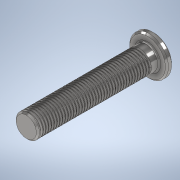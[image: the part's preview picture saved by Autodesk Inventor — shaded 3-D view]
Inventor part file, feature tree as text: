
AUTODESK INVENTOR PART (.ipt)
format: ipt  version: 2021 (Build 250183000, 183)  size: 1,093,632 bytes
history: native  units: in
note: dims shown in document units (in); Inventor stores cm internally (conversion verified against a paired STEP export)
features: sketch x5, extrude x4, chamfer x3, fillet x2, helix x1, projected_geometry x1
ambient origin geometry x8: Origin, YZ Plane, XZ Plane, XY Plane, X Axis, Y Axis, Z Axis, Center Point
bodies: Solid2 (feature_tree)
feature tree (16):
  extrude  "Extrusion3"  Depth=0.3085in TaperAngle=0.0deg
  chamfer  "Chamfer1"  Distance=0.0039in Angle=45.0deg
  extrude  "Extrusion4"  Depth=0.0157in TaperAngle=0.0deg
  fillet  "Fillet1"  Radius=0.0039in
  chamfer  "Chamfer2"  Distance=0.0039in Angle=45.0deg
  chamfer  "Chamfer3"  Distance=0.0039in Angle=45.0deg
  extrude  "Extrusion5"  Depth=0.0118in
  helix  "Coil1"  [1 undecoded]
  fillet  "Fillet3"  Radius=0.0591in
  extrude  "Extrusion6"  TaperAngle=60.0deg  [1 undecoded]
  sketch  "Sketch3"  dims[d6=0.0591in d7=0.3085in d8=0.0in d9=0.0039in d10=0.0787in d11=45.0deg]
  sketch  "Sketch4"  dims[d12=0.0984in d13=0.0157in d14=0.0in d15=0.0039in d17=0.0039in d18=0.0787in d19=45.0deg d20=0.0039in d21=0.0787in d22=45.0deg]
  sketch  "Sketch5"  dims[d23=0.0079in d24=0.0in d25=0.0118in d26=0.0118in d27=0.0591in]
  sketch  "Sketch6"  dims[d32=0.0197in d33=60.0deg]
  sketch  "Sketch7"  dims[d35=0.0039in d36=0.002in d37=0.0071in d38=0.3937in d39=15.5512in d40=0.0in d41=90.0deg d42=90.0deg d43=0.0in d44=0.0in d45=0.0039in d46=0.0236in d47=0.0in]
  projected_geometry  "Projected Loop1"
note: 2 required parameter values undecoded (feature->parameter linkage not recoverable at this tier; creation-order binding heuristic only, values carry confidence <= 0.55)
